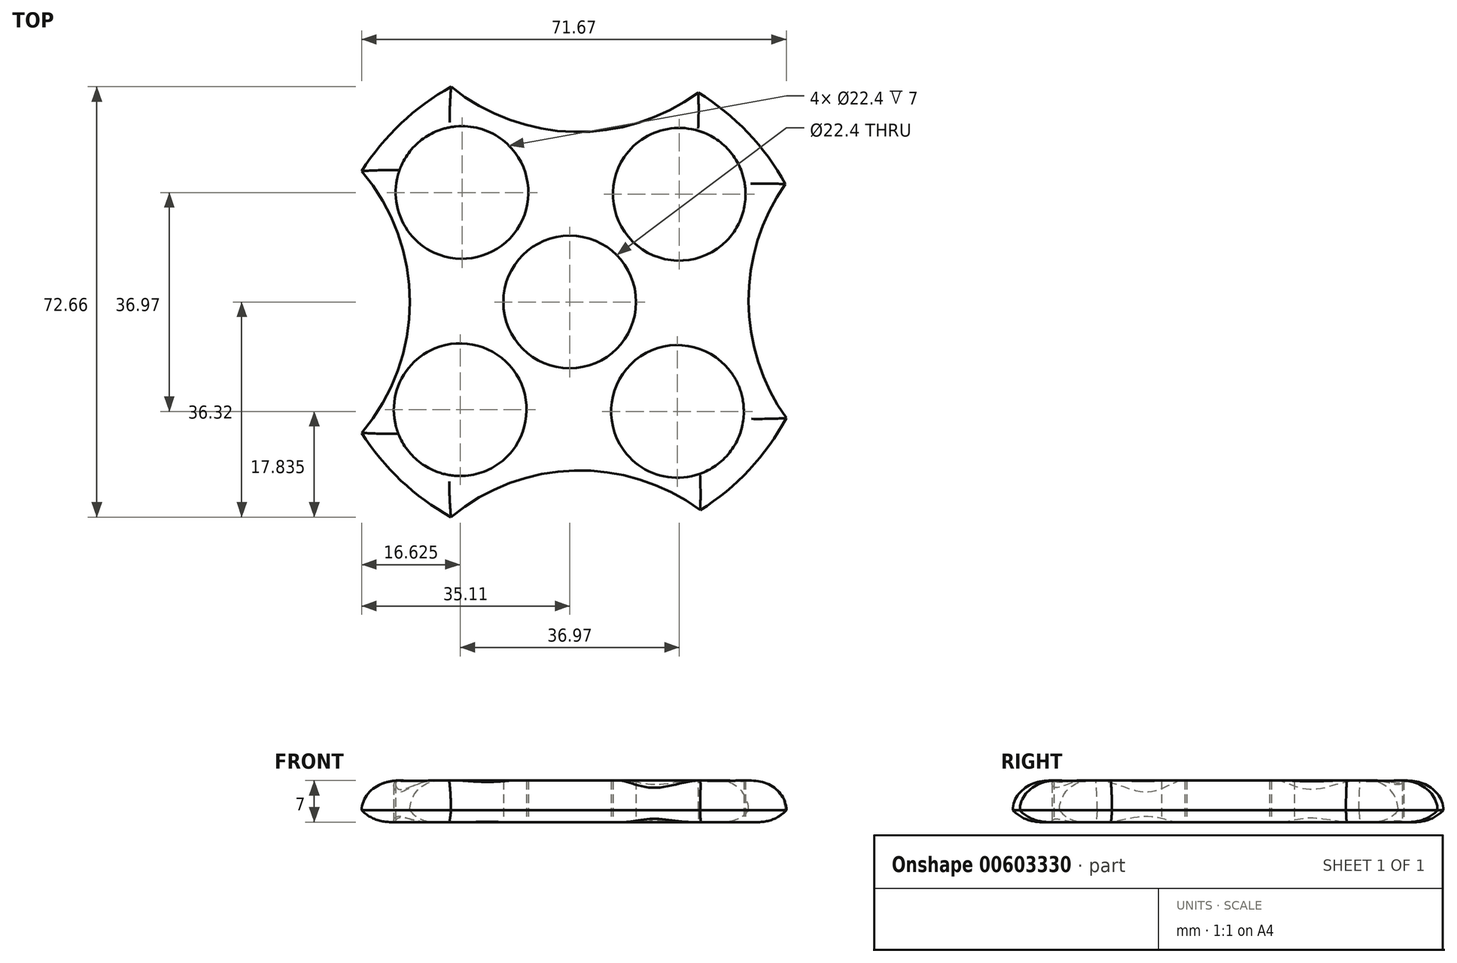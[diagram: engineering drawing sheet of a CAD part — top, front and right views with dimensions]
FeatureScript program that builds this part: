
annotation { "Feature Type Name" : "Feature", "Feature Type Description" : "" }
export const myFeature = defineFeature(function(context is Context, id is Id, definition is map)
    precondition{}
    {
        {
            var Q0;
            Q0=qCreatedBy(makeId("Top.planeOp"),FACE);
            var sketch = newSketch(context, id + "F0", { "sketchPlane" : qUnion([Q0])});
            skCircle(sketch, "E0", {"center": v(0, 0) * mm, "radius": 11.2 * mm});
            skArc(sketch, "E1", {"start": v(-35.11, -22.1) * mm, "mid": v(-28.48, -30.16) * mm, "end": v(-20.05, -36.32) * mm});
            skArc(sketch, "E2", {"start": v(-35.11, -22.1) * mm, "mid": v(-26.98, 0) * mm, "end": v(-35.11, 22.1) * mm});
            skArc(sketch, "E3.1.0", {"start": v(23.82, -36.59) * mm, "mid": v(1.73, -28.45) * mm, "end": v(-20.36, -36.59) * mm});
            skArc(sketch, "E3.2.0", {"start": v(38.31, 22.35) * mm, "mid": v(30.18, 0.26) * mm, "end": v(38.31, -21.84) * mm});
            skArc(sketch, "E3.3.0", {"start": v(-20.62, 36.84) * mm, "mid": v(1.47, 28.71) * mm, "end": v(23.56, 36.84) * mm});
            skPoint(sketch, "E3.center", {"position": v(1.6, 0.13) * mm});
            skCircle(sketch, "E4", {"center": v(-18.49, -18.18) * mm, "radius": 11.2 * mm});
            skCircle(sketch, "E5.1.0", {"center": v(18.18, -18.49) * mm, "radius": 11.2 * mm});
            skCircle(sketch, "E5.2.0", {"center": v(18.49, 18.18) * mm, "radius": 11.2 * mm});
            skCircle(sketch, "E5.3.0", {"center": v(-18.18, 18.49) * mm, "radius": 11.2 * mm});
            skArc(sketch, "E6.trimOffspring", {"start": v(-20.01, 36.34) * mm, "mid": v(-28.47, 30.18) * mm, "end": v(-35.11, 22.1) * mm});
            skArc(sketch, "E7.trimOffspring", {"start": v(36.4, 19.9) * mm, "mid": v(30.06, 28.59) * mm, "end": v(21.7, 35.36) * mm});
            skArc(sketch, "E8.trimOffspring", {"start": v(22.02, -35.16) * mm, "mid": v(30.31, -28.33) * mm, "end": v(36.56, -19.6) * mm});
            skSolve(sketch);
        }
        {
            var Q0;
            Q0=makeQuery(id+"F0.imprint","IMPRINT",FACE,{"disambiguationData":[TD([[makeQuery(id+"F0.imprint","IMPRINT",EDGE,{"derivedFrom":sQuery(id+"F0.wireOp",EDGE,"E0")}),-1.0]])]});
            extrude(context, id + "F1", {"entities" : qUnion([Q0]), "depth" : 7 * mm, "offsetDistance" : 25 * mm});
        }
        {
            var Q0;
            Q0=makeQuery(id+"F1.opExtrude","CAP_EDGE",EDGE,{"disambiguationData":[OSD([sQuery(id+"F0.wireOp",EDGE,"E3.3.0")])],"isStart":false});
            var Q1;
            Q1=makeQuery(id+"F1.opExtrude","CAP_EDGE",EDGE,{"disambiguationData":[OSD([sQuery(id+"F0.wireOp",EDGE,"E7.trimOffspring")])],"isStart":false});
            var Q2;
            Q2=makeQuery(id+"F1.opExtrude","CAP_EDGE",EDGE,{"disambiguationData":[OSD([sQuery(id+"F0.wireOp",EDGE,"E3.2.0")])],"isStart":false});
            var Q3;
            Q3=makeQuery(id+"F1.opExtrude","CAP_EDGE",EDGE,{"disambiguationData":[OSD([sQuery(id+"F0.wireOp",EDGE,"E8.trimOffspring")])],"isStart":false});
            var Q4;
            Q4=makeQuery(id+"F1.opExtrude","CAP_EDGE",EDGE,{"disambiguationData":[OSD([sQuery(id+"F0.wireOp",EDGE,"E3.1.0")])],"isStart":false});
            var Q5;
            Q5=makeQuery(id+"F1.opExtrude","CAP_EDGE",EDGE,{"disambiguationData":[OSD([sQuery(id+"F0.wireOp",EDGE,"E1")])],"isStart":false});
            var Q6;
            Q6=makeQuery(id+"F1.opExtrude","CAP_EDGE",EDGE,{"disambiguationData":[OSD([sQuery(id+"F0.wireOp",EDGE,"E2")])],"isStart":false});
            var Q7;
            Q7=makeQuery(id+"F1.opExtrude","CAP_EDGE",EDGE,{"disambiguationData":[OSD([sQuery(id+"F0.wireOp",EDGE,"E6.trimOffspring")])],"isStart":false});
            fillet(context, id + "F2", {"entities" : qUnion([Q0, Q1, Q2, Q3, Q4, Q5, Q6, Q7]), "radius" : 5 * mm, "tangentPropagation" : true, "allowEdgeOverflow" : false});
        }
        {
            var Q0;
            Q0=makeQuery(id+"F1.opExtrude","CAP_EDGE",EDGE,{"disambiguationData":[OSD([sQuery(id+"F0.wireOp",EDGE,"E3.1.0")])],"isStart":true});
            var Q1;
            Q1=makeQuery(id+"F1.opExtrude","CAP_EDGE",EDGE,{"disambiguationData":[OSD([sQuery(id+"F0.wireOp",EDGE,"E1")])],"isStart":true});
            var Q2;
            Q2=makeQuery(id+"F1.opExtrude","CAP_EDGE",EDGE,{"disambiguationData":[OSD([sQuery(id+"F0.wireOp",EDGE,"E2")])],"isStart":true});
            var Q3;
            Q3=makeQuery(id+"F1.opExtrude","CAP_EDGE",EDGE,{"disambiguationData":[OSD([sQuery(id+"F0.wireOp",EDGE,"E6.trimOffspring")])],"isStart":true});
            var Q4;
            Q4=makeQuery(id+"F1.opExtrude","CAP_EDGE",EDGE,{"disambiguationData":[OSD([sQuery(id+"F0.wireOp",EDGE,"E3.3.0")])],"isStart":true});
            var Q5;
            Q5=makeQuery(id+"F1.opExtrude","CAP_EDGE",EDGE,{"disambiguationData":[OSD([sQuery(id+"F0.wireOp",EDGE,"E7.trimOffspring")])],"isStart":true});
            var Q6;
            Q6=makeQuery(id+"F1.opExtrude","CAP_EDGE",EDGE,{"disambiguationData":[OSD([sQuery(id+"F0.wireOp",EDGE,"E3.2.0")])],"isStart":true});
            var Q7;
            Q7=makeQuery(id+"F1.opExtrude","CAP_EDGE",EDGE,{"disambiguationData":[OSD([sQuery(id+"F0.wireOp",EDGE,"E8.trimOffspring")])],"isStart":true});
            fillet(context, id + "F3", {"entities" : qUnion([Q0, Q1, Q2, Q3, Q4, Q5, Q6, Q7]), "radius" : 5 * mm, "tangentPropagation" : true, "allowEdgeOverflow" : false});
        }
    });
